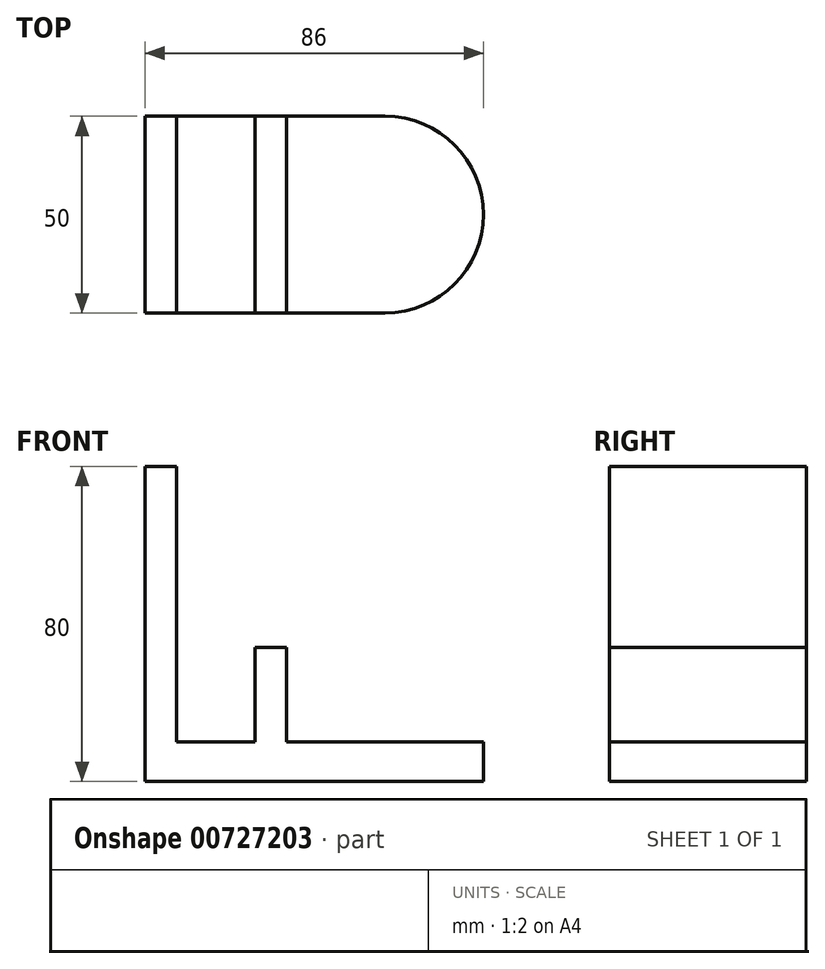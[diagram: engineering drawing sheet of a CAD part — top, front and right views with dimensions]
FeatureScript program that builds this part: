
annotation { "Feature Type Name" : "Feature", "Feature Type Description" : "" }
export const myFeature = defineFeature(function(context is Context, id is Id, definition is map)
    precondition{}
    {
        {
            var Q0;
            Q0=qCreatedBy(makeId("Front.planeOp"),FACE);
            var sketch = newSketch(context, id + "F0", { "sketchPlane" : qUnion([Q0])});
            skLineSegment(sketch, "E0", {"start": v(0, 0) * mm, "end": v(0, 80) * mm});
            skLineSegment(sketch, "E1", {"start": v(0, 80) * mm, "end": v(8, 80) * mm});
            skLineSegment(sketch, "E2", {"start": v(8, 80) * mm, "end": v(8, 10) * mm});
            skLineSegment(sketch, "E3", {"start": v(8, 10) * mm, "end": v(28, 10) * mm});
            skLineSegment(sketch, "E4", {"start": v(28, 10) * mm, "end": v(28, 34) * mm});
            skLineSegment(sketch, "E5", {"start": v(28, 34) * mm, "end": v(36, 34) * mm});
            skLineSegment(sketch, "E6", {"start": v(36, 34) * mm, "end": v(36, 10) * mm});
            skLineSegment(sketch, "E7", {"start": v(36, 10) * mm, "end": v(61, 10) * mm});
            skLineSegment(sketch, "E8", {"start": v(61, 10) * mm, "end": v(86, 10) * mm});
            skLineSegment(sketch, "E9", {"start": v(86, 10) * mm, "end": v(86, 0) * mm});
            skLineSegment(sketch, "E10", {"start": v(86, 0) * mm, "end": v(0, 0) * mm});
            skSolve(sketch);
        }
        {
            var Q0;
            Q0=makeQuery(id+"F0.imprint","IMPRINT",FACE,{"disambiguationData":[TD([[makeQuery(id+"F0.imprint","IMPRINT",EDGE,{"derivedFrom":sQuery(id+"F0.wireOp",EDGE,"E0")}),-1.0]])]});
            var sketch = newSketch(context, id + "F1", { "sketchPlane" : qUnion([Q0])});
            skSolve(sketch);
        }
        {
            var Q0;
            Q0=makeQuery(id+"F1.imprint","IMPRINT",FACE,{"disambiguationData":[TD([[makeQuery(id+"F1.imprint","IMPRINT",EDGE,{"derivedFrom":makeQuery(id+"F0.imprint","IMPRINT",EDGE,{"derivedFrom":sQuery(id+"F0.wireOp",EDGE,"E0")})}),-1.0]])]});
            extrude(context, id + "F2", {"entities" : qUnion([Q0]), "depth" : 50 * mm, "offsetDistance" : 25 * mm});
        }
        {
            var Q0;
            Q0=makeQuery(id+"F2.opExtrude","CAP_EDGE",EDGE,{"disambiguationData":[OSD([sQuery(id+"F0.wireOp",EDGE,"E9")])],"isStart":false});
            fillet(context, id + "F3", {"entities" : qUnion([Q0]), "radius" : 25 * mm, "tangentPropagation" : true, "allowEdgeOverflow" : false});
        }
        {
            var Q0;
            Q0=makeQuery(id+"F2.opExtrude","CAP_EDGE",EDGE,{"disambiguationData":[OSD([sQuery(id+"F0.wireOp",EDGE,"E9")])],"isStart":true});
            fillet(context, id + "F4", {"entities" : qUnion([Q0]), "radius" : 25 * mm, "tangentPropagation" : true, "allowEdgeOverflow" : false});
        }
    });
